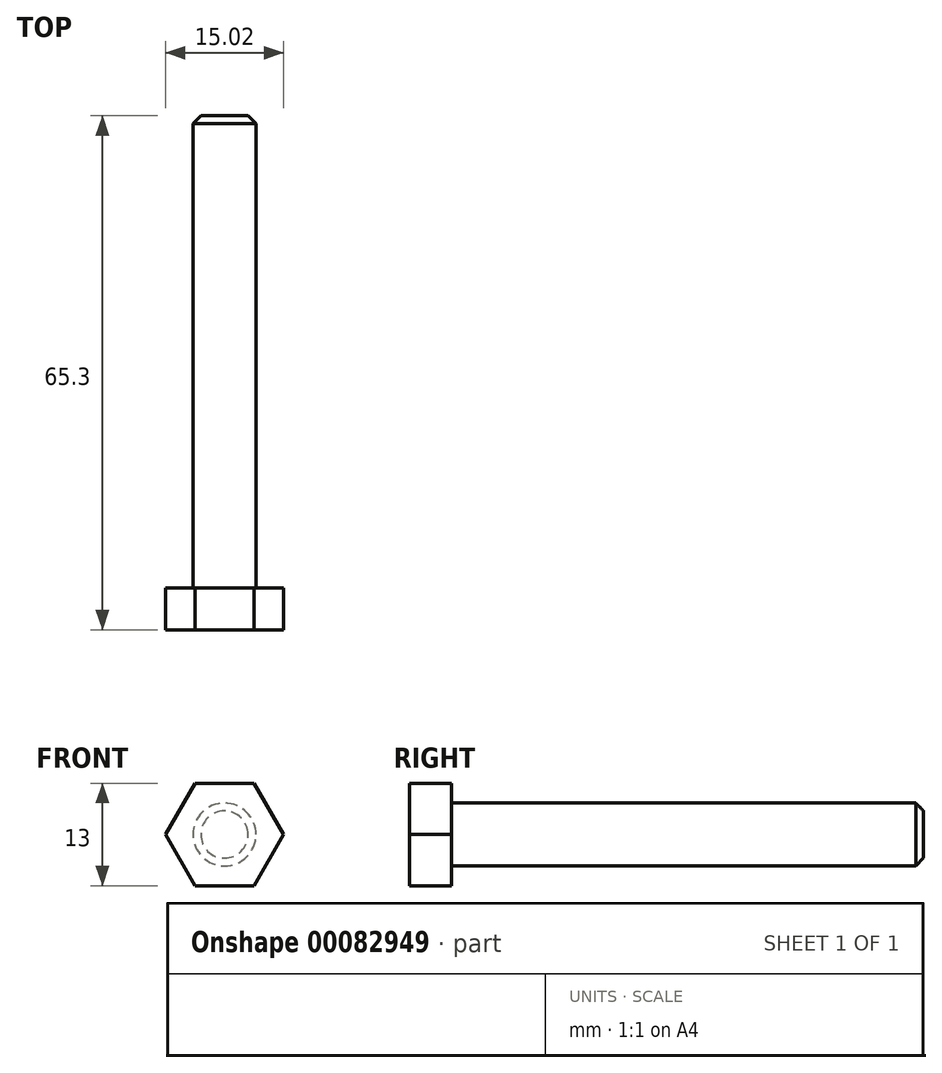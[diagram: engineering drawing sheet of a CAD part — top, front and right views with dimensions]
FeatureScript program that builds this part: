
annotation { "Feature Type Name" : "Feature", "Feature Type Description" : "" }
export const myFeature = defineFeature(function(context is Context, id is Id, definition is map)
    precondition{}
    {
        {
            var Q0;
            Q0=qCreatedBy(makeId("Front.planeOp"),FACE);
            var sketch = newSketch(context, id + "F0", { "sketchPlane" : qUnion([Q0])});
            skCircle(sketch, "E0.cCircle", {"center": v(0, 0) * mm, "radius": 7.5 * mm, "construction": true});
            skLineSegment(sketch, "E0.0", {"start": v(7.5, 0) * mm, "end": v(3.75, -6.5) * mm});
            skLineSegment(sketch, "E0.1", {"start": v(3.75, -6.5) * mm, "end": v(-3.75, -6.5) * mm});
            skLineSegment(sketch, "E0.2", {"start": v(-3.75, -6.5) * mm, "end": v(-7.5, 0) * mm});
            skLineSegment(sketch, "E0.3", {"start": v(-7.5, 0) * mm, "end": v(-3.75, 6.5) * mm});
            skLineSegment(sketch, "E0.4", {"start": v(-3.75, 6.5) * mm, "end": v(3.75, 6.5) * mm});
            skLineSegment(sketch, "E0.5", {"start": v(3.75, 6.5) * mm, "end": v(7.5, 0) * mm});
            skSolve(sketch);
        }
        {
            var Q0;
            Q0=makeQuery(id+"F0.imprint","IMPRINT",FACE,{"disambiguationData":[TD([[makeQuery(id+"F0.imprint","IMPRINT",EDGE,{"derivedFrom":sQuery(id+"F0.wireOp",EDGE,"E0.0")}),-1.0]])]});
            extrude(context, id + "F1", {"entities" : qUnion([Q0]), "depth" : 5.3 * mm});
        }
        {
            var Q0;
            Q0=makeQuery(id+"F1.opExtrude","CAP_FACE",FACE,{"disambiguationData":[OSD([sQuery(id+"F0.wireOp",EDGE,"E0.0"),sQuery(id+"F0.wireOp",EDGE,"E0.1"),sQuery(id+"F0.wireOp",EDGE,"E0.2"),sQuery(id+"F0.wireOp",EDGE,"E0.3"),sQuery(id+"F0.wireOp",EDGE,"E0.4"),sQuery(id+"F0.wireOp",EDGE,"E0.5")])],"isStart":true});
            var sketch = newSketch(context, id + "F2", { "sketchPlane" : qUnion([Q0])});
            skCircle(sketch, "E1", {"center": v(0, 0) * mm, "radius": 4 * mm});
            skSolve(sketch);
        }
        {
            var Q0;
            Q0=makeQuery(id+"F2.imprint","IMPRINT",FACE,{"disambiguationData":[TD([[makeQuery(id+"F2.imprint","IMPRINT",EDGE,{"derivedFrom":sQuery(id+"F2.wireOp",EDGE,"E1")}),1.0]])]});
            extrude(context, id + "F3", {"entities" : qUnion([Q0]), "operationType" : NewBodyOperationType.ADD, "depth" : 60 * mm});
        }
        {
            var Q0;
            Q0=makeQuery(id+"F3.opExtrude","CAP_EDGE",EDGE,{"disambiguationData":[OSD([sQuery(id+"F2.wireOp",EDGE,"E1")])],"isStart":false});
            chamfer(context, id + "F4", {"entities" : qUnion([Q0]), "width" : 1 * mm, "tangentPropagation" : true});
        }
    });
